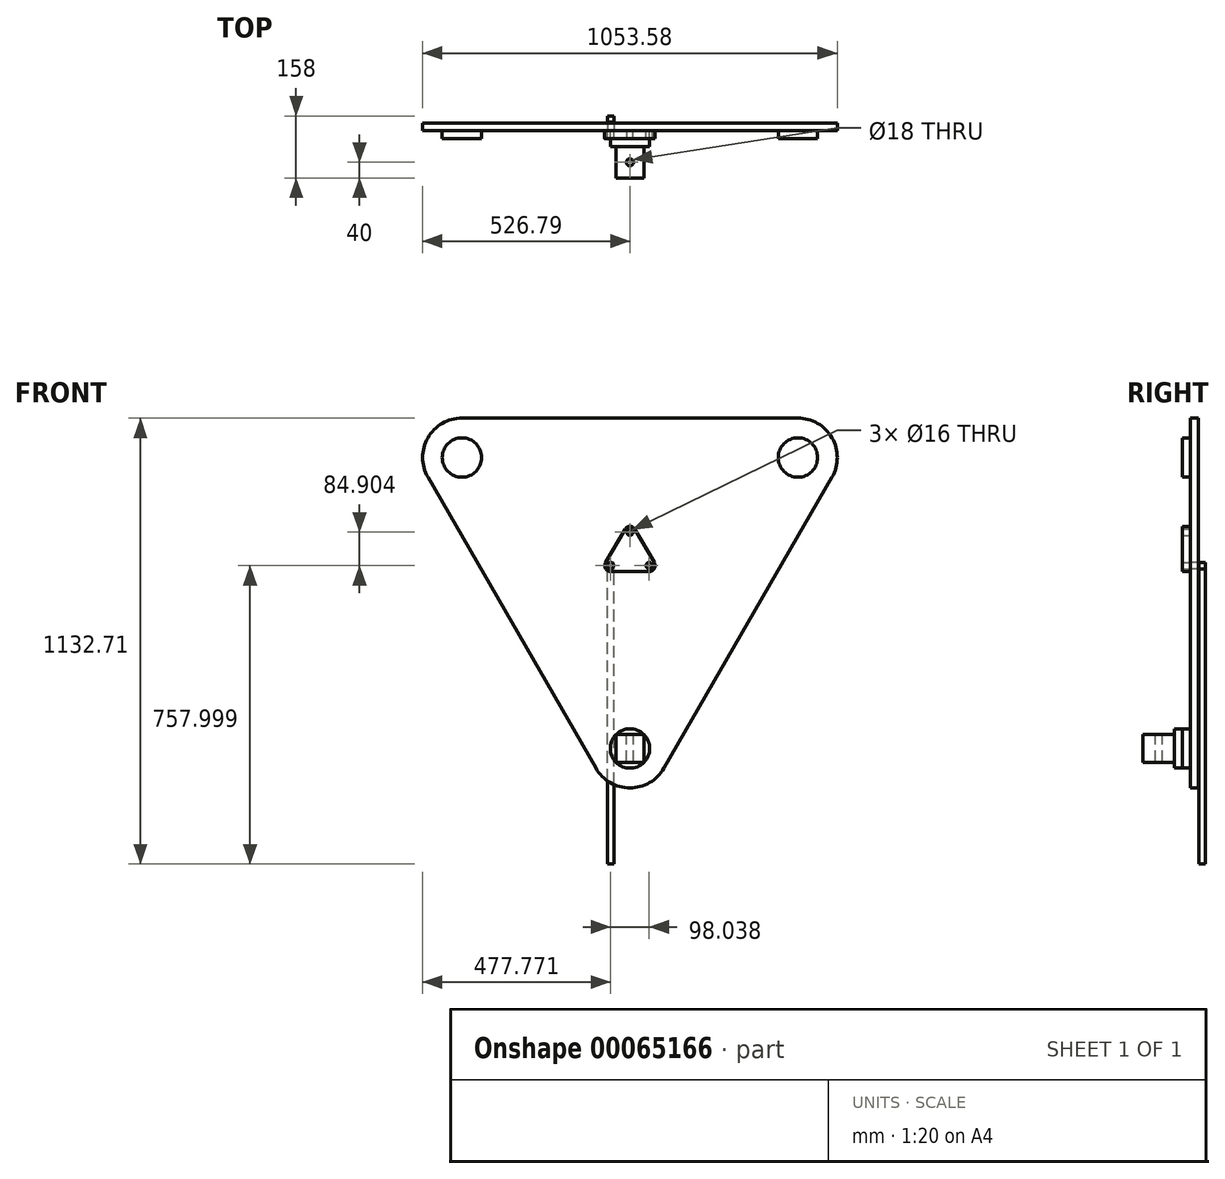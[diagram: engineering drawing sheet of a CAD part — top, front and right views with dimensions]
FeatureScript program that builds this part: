
annotation { "Feature Type Name" : "Feature", "Feature Type Description" : "" }
export const myFeature = defineFeature(function(context is Context, id is Id, definition is map)
    precondition{}
    {
        {
            var Q0;
            Q0=qCreatedBy(makeId("Front.planeOp"),FACE);
            var sketch = newSketch(context, id + "F0", { "sketchPlane" : qUnion([Q0])});
            skCircle(sketch, "E0.cCircle", {"center": v(0, 0) * mm, "radius": 43.3 * mm, "construction": true});
            skLineSegment(sketch, "E0.0", {"start": v(-62, -20.8) * mm, "end": v(-13, 64.1) * mm});
            skLineSegment(sketch, "E0.1", {"start": v(13, 64.1) * mm, "end": v(62, -20.8) * mm});
            skLineSegment(sketch, "E0.2", {"start": v(49.02, -43.3) * mm, "end": v(-49.02, -43.3) * mm});
            skPoint(sketch, "E0.0.midPoint", {"position": v(-37.5, 21.65) * mm});
            skPoint(sketch, "E1.visualSharp", {"position": v(75, -43.3) * mm});
            skArc(sketch, "E1.filletArc", {"start": v(49.02, -43.3) * mm, "mid": v(62, -35.8) * mm, "end": v(62, -20.8) * mm});
            skPoint(sketch, "E2.visualSharp", {"position": v(-75, -43.3) * mm});
            skArc(sketch, "E2.filletArc", {"start": v(-62, -20.8) * mm, "mid": v(-62, -35.8) * mm, "end": v(-49.02, -43.3) * mm});
            skPoint(sketch, "E3.visualSharp", {"position": v(0, 86.6) * mm});
            skArc(sketch, "E3.filletArc", {"start": v(13, 64.1) * mm, "mid": v(0, 71.6) * mm, "end": v(-13, 64.1) * mm});
            skCircle(sketch, "E4", {"center": v(49.02, -28.3) * mm, "radius": 8 * mm});
            skCircle(sketch, "E5", {"center": v(-49.02, -28.3) * mm, "radius": 8 * mm});
            skCircle(sketch, "E6", {"center": v(0, 56.6) * mm, "radius": 8 * mm});
            skSolve(sketch);
        }
        {
            var Q0;
            Q0=qSketchRegion(id+"F0",true);
            extrude(context, id + "F1", {"entities" : qUnion([Q0]), "depth" : 20 * mm});
        }
        {
            var Q0;
            Q0=makeQuery(id+"F1.opExtrude","CAP_FACE",FACE,{"disambiguationData":[OSD([sQuery(id+"F0.wireOp",EDGE,"E0.0"),sQuery(id+"F0.wireOp",EDGE,"E0.1"),sQuery(id+"F0.wireOp",EDGE,"E0.2"),sQuery(id+"F0.wireOp",EDGE,"E1.filletArc"),sQuery(id+"F0.wireOp",EDGE,"E2.filletArc"),sQuery(id+"F0.wireOp",EDGE,"E3.filletArc"),sQuery(id+"F0.wireOp",EDGE,"E4"),sQuery(id+"F0.wireOp",EDGE,"E5"),sQuery(id+"F0.wireOp",EDGE,"E6")])],"isStart":true});
            var sketch = newSketch(context, id + "F2", { "sketchPlane" : qUnion([Q0])});
            skCircle(sketch, "E7", {"center": v(49.02, -28.3) * mm, "radius": 8 * mm});
            skSolve(sketch);
        }
        {
            var Q0;
            Q0=qSketchRegion(id+"F2",true);
            extrude(context, id + "F3", {"entities" : qUnion([Q0]), "depth" : 22 * mm});
        }
        {
            var Q0;
            Q0=makeQuery(id+"F3.opExtrude","CAP_FACE",FACE,{"disambiguationData":[OSD([sQuery(id+"F2.wireOp",EDGE,"E7")])],"isStart":false});
            var sketch = newSketch(context, id + "F4", { "sketchPlane" : qUnion([Q0])});
            skLineSegment(sketch, "E8.bottom", {"start": v(41.02, -36.3) * mm, "end": v(57.02, -36.3) * mm});
            skLineSegment(sketch, "E8.top", {"start": v(41.02, -20.3) * mm, "end": v(57.02, -20.3) * mm});
            skLineSegment(sketch, "E8.left", {"start": v(57.02, -36.3) * mm, "end": v(57.02, -20.3) * mm});
            skLineSegment(sketch, "E8.right", {"start": v(41.02, -36.3) * mm, "end": v(41.02, -20.3) * mm});
            skSolve(sketch);
        }
        {
            var Q0;
            Q0=qSketchRegion(id+"F4",true);
            extrude(context, id + "F5", {"entities" : qUnion([Q0]), "operationType" : NewBodyOperationType.ADD, "depth" : 16 * mm});
        }
        {
            var Q0;
            Q0=makeQuery(id+"F5.opExtrude","SWEPT_FACE",FACE,{"disambiguationData":[OSD([sQuery(id+"F4.wireOp",EDGE,"E8.bottom")])]});
            var sketch = newSketch(context, id + "F6", { "sketchPlane" : qUnion([Q0])});
            skCircle(sketch, "E9", {"center": v(-49.02, -30) * mm, "radius": 8 * mm});
            skPoint(sketch, "E9.centerSnap0", {"position": v(-57.02, -30) * mm});
            skSolve(sketch);
        }
        {
            var Q0;
            Q0=qSketchRegion(id+"F6",true);
            extrude(context, id + "F7", {"entities" : qUnion([Q0]), "operationType" : NewBodyOperationType.ADD, "depth" : 750 * mm});
        }
        {
            var Q0;
            Q0=makeQuery(id+"F1.opExtrude","CAP_FACE",FACE,{"disambiguationData":[OSD([sQuery(id+"F0.wireOp",EDGE,"E0.0"),sQuery(id+"F0.wireOp",EDGE,"E0.1"),sQuery(id+"F0.wireOp",EDGE,"E0.2"),sQuery(id+"F0.wireOp",EDGE,"E1.filletArc"),sQuery(id+"F0.wireOp",EDGE,"E2.filletArc"),sQuery(id+"F0.wireOp",EDGE,"E3.filletArc"),sQuery(id+"F0.wireOp",EDGE,"E4"),sQuery(id+"F0.wireOp",EDGE,"E5"),sQuery(id+"F0.wireOp",EDGE,"E6")])],"isStart":true});
            var sketch = newSketch(context, id + "F8", { "sketchPlane" : qUnion([Q0])});
            skCircle(sketch, "E10.cCircle", {"center": v(0, 0) * mm, "radius": 346.41 * mm, "construction": true});
            skLineSegment(sketch, "E10.0", {"start": v(513.4, 196.41) * mm, "end": v(86.6, -542.82) * mm});
            skLineSegment(sketch, "E10.1", {"start": v(-86.6, -542.82) * mm, "end": v(-513.4, 196.41) * mm});
            skLineSegment(sketch, "E10.2", {"start": v(-426.8, 346.41) * mm, "end": v(426.8, 346.41) * mm});
            skPoint(sketch, "E10.0.midPoint", {"position": v(300, -173.2) * mm});
            skPoint(sketch, "E11.visualSharp", {"position": v(-600, 346.41) * mm});
            skArc(sketch, "E11.filletArc", {"start": v(-426.8, 346.41) * mm, "mid": v(-513.4, 296.41) * mm, "end": v(-513.4, 196.41) * mm});
            skPoint(sketch, "E12.visualSharp", {"position": v(600, 346.41) * mm});
            skArc(sketch, "E12.filletArc", {"start": v(513.4, 196.41) * mm, "mid": v(513.4, 296.41) * mm, "end": v(426.8, 346.41) * mm});
            skPoint(sketch, "E13.visualSharp", {"position": v(0, -692.82) * mm});
            skArc(sketch, "E13.filletArc", {"start": v(-86.6, -542.82) * mm, "mid": v(0, -592.82) * mm, "end": v(86.6, -542.82) * mm});
            skSolve(sketch);
        }
        {
            var Q0;
            Q0=qSketchRegion(id+"F8",true);
            extrude(context, id + "F9", {"entities" : qUnion([Q0]), "depth" : 20 * mm});
        }
        {
            var Q0;
            Q0=makeQuery(id+"F9.opExtrude","CAP_FACE",FACE,{"disambiguationData":[OSD([sQuery(id+"F8.wireOp",EDGE,"E10.0"),sQuery(id+"F8.wireOp",EDGE,"E10.1"),sQuery(id+"F8.wireOp",EDGE,"E10.2"),sQuery(id+"F8.wireOp",EDGE,"E11.filletArc"),sQuery(id+"F8.wireOp",EDGE,"E12.filletArc"),sQuery(id+"F8.wireOp",EDGE,"E13.filletArc")])],"isStart":true});
            var sketch = newSketch(context, id + "F10", { "sketchPlane" : qUnion([Q0])});
            skCircle(sketch, "E14", {"center": v(0, -492.82) * mm, "radius": 50 * mm});
            skCircle(sketch, "E15", {"center": v(-426.8, 246.41) * mm, "radius": 50 * mm});
            skCircle(sketch, "E16", {"center": v(426.8, 246.41) * mm, "radius": 50 * mm});
            skSolve(sketch);
        }
        {
            var Q0;
            Q0=qSketchRegion(id+"F10",true);
            extrude(context, id + "F11", {"entities" : qUnion([Q0]), "operationType" : NewBodyOperationType.ADD, "depth" : 20 * mm});
        }
        {
            var Q0;
            Q0=makeQuery(id+"F11.opExtrude","CAP_FACE",FACE,{"disambiguationData":[OSD([sQuery(id+"F10.wireOp",EDGE,"E14")])],"isStart":false});
            var sketch = newSketch(context, id + "F12", { "sketchPlane" : qUnion([Q0])});
            skCircle(sketch, "E17", {"center": v(0, -492.82) * mm, "radius": 50 * mm});
            skSolve(sketch);
        }
        {
            var Q0;
            Q0=qSketchRegion(id+"F12",true);
            extrude(context, id + "F13", {"entities" : qUnion([Q0]), "depth" : 20 * mm});
        }
        {
            var Q0;
            Q0=makeQuery(id+"F13.opExtrude","CAP_FACE",FACE,{"disambiguationData":[OSD([sQuery(id+"F12.wireOp",EDGE,"E17")])],"isStart":false});
            var sketch = newSketch(context, id + "F14", { "sketchPlane" : qUnion([Q0])});
            skLineSegment(sketch, "E18.bottom", {"start": v(-35.36, -528.18) * mm, "end": v(35.36, -528.18) * mm});
            skLineSegment(sketch, "E18.top", {"start": v(-35.36, -457.46) * mm, "end": v(35.36, -457.46) * mm});
            skLineSegment(sketch, "E18.left", {"start": v(-35.36, -528.18) * mm, "end": v(-35.36, -457.46) * mm});
            skLineSegment(sketch, "E18.right", {"start": v(35.36, -528.18) * mm, "end": v(35.36, -457.46) * mm});
            skLineSegment(sketch, "E19", {"start": v(-35.36, -528.18) * mm, "end": v(35.36, -457.46) * mm});
            skSolve(sketch);
        }
        {
            var Q0;
            Q0=makeQuery(id+"F14.imprint","IMPRINT",FACE,{"disambiguationData":[TD([[makeQuery(id+"F14.imprint","IMPRINT",EDGE,{"derivedFrom":sQuery(id+"F14.wireOp",EDGE,"E18.bottom")}),1.0]])]});
            var Q1;
            Q1=makeQuery(id+"F14.imprint","IMPRINT",FACE,{"disambiguationData":[TD([[makeQuery(id+"F14.imprint","IMPRINT",EDGE,{"derivedFrom":sQuery(id+"F14.wireOp",EDGE,"E18.top")}),-1.0]])]});
            extrude(context, id + "F15", {"entities" : qUnion([Q0, Q1]), "operationType" : NewBodyOperationType.ADD, "depth" : 80 * mm});
        }
        {
            var Q0;
            Q0=makeQuery(id+"F15.opExtrude","SWEPT_FACE",FACE,{"disambiguationData":[OSD([sQuery(id+"F14.wireOp",EDGE,"E18.top")])]});
            var sketch = newSketch(context, id + "F16", { "sketchPlane" : qUnion([Q0])});
            skCircle(sketch, "E20", {"center": v(0, -80) * mm, "radius": 9 * mm});
            skLineSegment(sketch, "E21", {"start": v(-35.36, -80) * mm, "end": v(35.36, -80) * mm});
            skSolve(sketch);
        }
        {
            var Q0;
            Q0=qSketchRegion(id+"F16",true);
            extrude(context, id + "F17", {"entities" : qUnion([Q0]), "operationType" : NewBodyOperationType.REMOVE, "oppositeDirection" : true, "depth" : 100 * mm});
        }
    });
